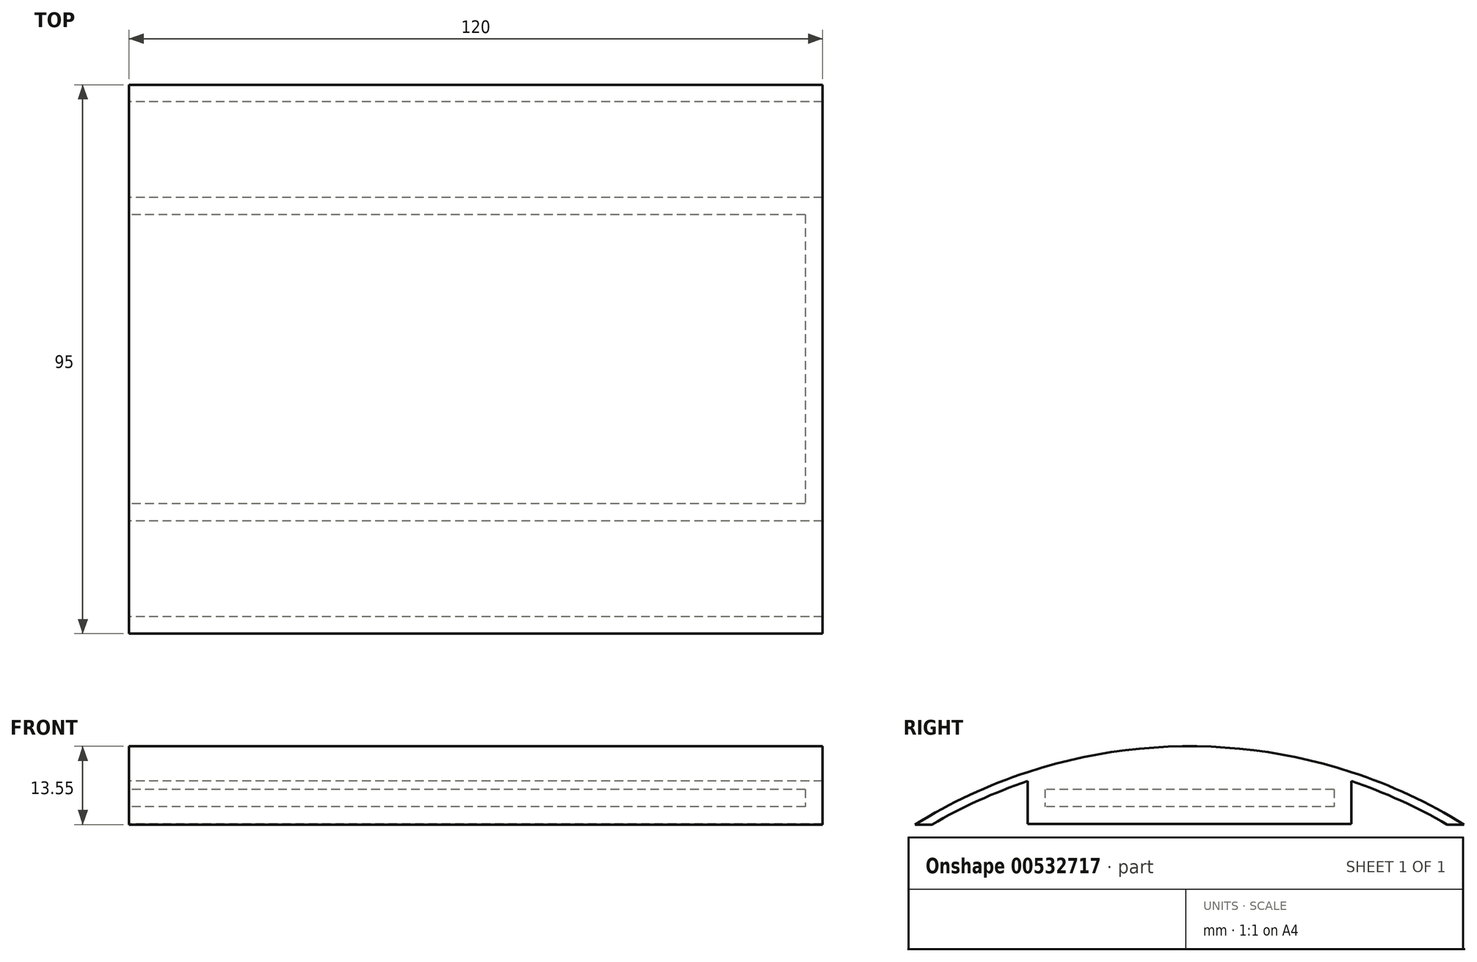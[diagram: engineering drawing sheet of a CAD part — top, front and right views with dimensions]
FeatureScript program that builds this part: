
annotation { "Feature Type Name" : "Feature", "Feature Type Description" : "" }
export const myFeature = defineFeature(function(context is Context, id is Id, definition is map)
    precondition{}
    {
        {
            var Q0;
            Q0=qCreatedBy(makeId("Right.planeOp"),FACE);
            var sketch = newSketch(context, id + "F0", { "sketchPlane" : qUnion([Q0])});
            skLineSegment(sketch, "E0.top", {"start": v(28, -4.5) * mm, "end": v(-28, -4.5) * mm});
            skLineSegment(sketch, "E0.left", {"start": v(28, 4.5) * mm, "end": v(28, -4.5) * mm});
            skLineSegment(sketch, "E0.right", {"start": v(-28, 4.5) * mm, "end": v(-28, -4.5) * mm});
            skArc(sketch, "E1", {"start": v(28, 4.5) * mm, "mid": v(0, 8.97) * mm, "end": v(-28, 4.5) * mm});
            skSolve(sketch);
        }
        {
            var Q0;
            Q0=qSketchRegion(id+"F0",true);
            extrude(context, id + "F1", {"entities" : qUnion([Q0]), "endBound" : BoundingType.SYMMETRIC, "depth" : 120 * mm});
        }
        {
            var Q0;
            Q0=makeQuery(id+"F1.opExtrude","CAP_FACE",FACE,{"disambiguationData":[OSD([sQuery(id+"F0.wireOp",EDGE,"E0.bottom"),sQuery(id+"F0.wireOp",EDGE,"E0.top"),sQuery(id+"F0.wireOp",EDGE,"E0.left"),sQuery(id+"F0.wireOp",EDGE,"E0.right"),sQuery(id+"F0.wireOp",EDGE,"g34ocrht-rPQt-wPrD-86mF-Q5vO9vs38KqS.bottom"),sQuery(id+"F0.wireOp",EDGE,"g34ocrht-rPQt-wPrD-86mF-Q5vO9vs38KqS.top"),sQuery(id+"F0.wireOp",EDGE,"g34ocrht-rPQt-wPrD-86mF-Q5vO9vs38KqS.left"),sQuery(id+"F0.wireOp",EDGE,"g34ocrht-rPQt-wPrD-86mF-Q5vO9vs38KqS.right")])],"isStart":true});
            var sketch = newSketch(context, id + "F2", { "sketchPlane" : qUnion([Q0])});
            skLineSegment(sketch, "E2.bottom", {"start": v(-28, -4.5) * mm, "end": v(28, -4.5) * mm});
            skLineSegment(sketch, "E2.top", {"start": v(-28, -4.5) * mm, "end": v(28, -4.5) * mm});
            skLineSegment(sketch, "E2.left", {"start": v(-28, -4.5) * mm, "end": v(-28, -4.5) * mm});
            skLineSegment(sketch, "E2.right", {"start": v(28, -4.5) * mm, "end": v(28, -4.5) * mm});
            skLineSegment(sketch, "E3.bottom", {"start": v(-25, 1.5) * mm, "end": v(25, 1.5) * mm});
            skLineSegment(sketch, "E3.top", {"start": v(-25, -1.5) * mm, "end": v(25, -1.5) * mm});
            skLineSegment(sketch, "E3.left", {"start": v(-25, 1.5) * mm, "end": v(-25, -1.5) * mm});
            skLineSegment(sketch, "E3.right", {"start": v(25, 1.5) * mm, "end": v(25, -1.5) * mm});
            skPoint(sketch, "E3.middle", {"position": v(0, 0) * mm});
            skSolve(sketch);
        }
        {
            var Q0;
            Q0=qSketchRegion(id+"F2",true);
            extrude(context, id + "F3", {"entities" : qUnion([Q0]), "operationType" : NewBodyOperationType.REMOVE, "oppositeDirection" : true, "depth" : 117 * mm});
        }
        {
            var Q0;
            Q0=qCreatedBy(makeId("Right.planeOp"),FACE);
            var sketch = newSketch(context, id + "F4", { "sketchPlane" : qUnion([Q0])});
            skArc(sketch, "E4", {"start": v(47.5, -4.58) * mm, "mid": v(0, 8.97) * mm, "end": v(-47.5, -4.58) * mm});
            skArc(sketch, "E5", {"start": v(44.59, -4.58) * mm, "mid": v(0, 7.47) * mm, "end": v(-44.59, -4.58) * mm});
            skLineSegment(sketch, "E6", {"start": v(44.59, -4.58) * mm, "end": v(47.5, -4.58) * mm});
            skLineSegment(sketch, "E7", {"start": v(-44.59, -4.58) * mm, "end": v(-47.5, -4.58) * mm});
            skLineSegment(sketch, "E8", {"start": v(-47.5, -4.58) * mm, "end": v(-44.59, -4.58) * mm});
            skSolve(sketch);
        }
        {
            var Q0;
            Q0=makeQuery(id+"F4.imprint","IMPRINT",FACE,{"disambiguationData":[TD([[makeQuery(id+"F4.imprint","IMPRINT",EDGE,{"derivedFrom":sQuery(id+"F4.wireOp",EDGE,"E4")}),1.0]])]});
            extrude(context, id + "F5", {"entities" : qUnion([Q0]), "operationType" : NewBodyOperationType.ADD, "endBound" : BoundingType.SYMMETRIC, "depth" : 120 * mm});
        }
    });
